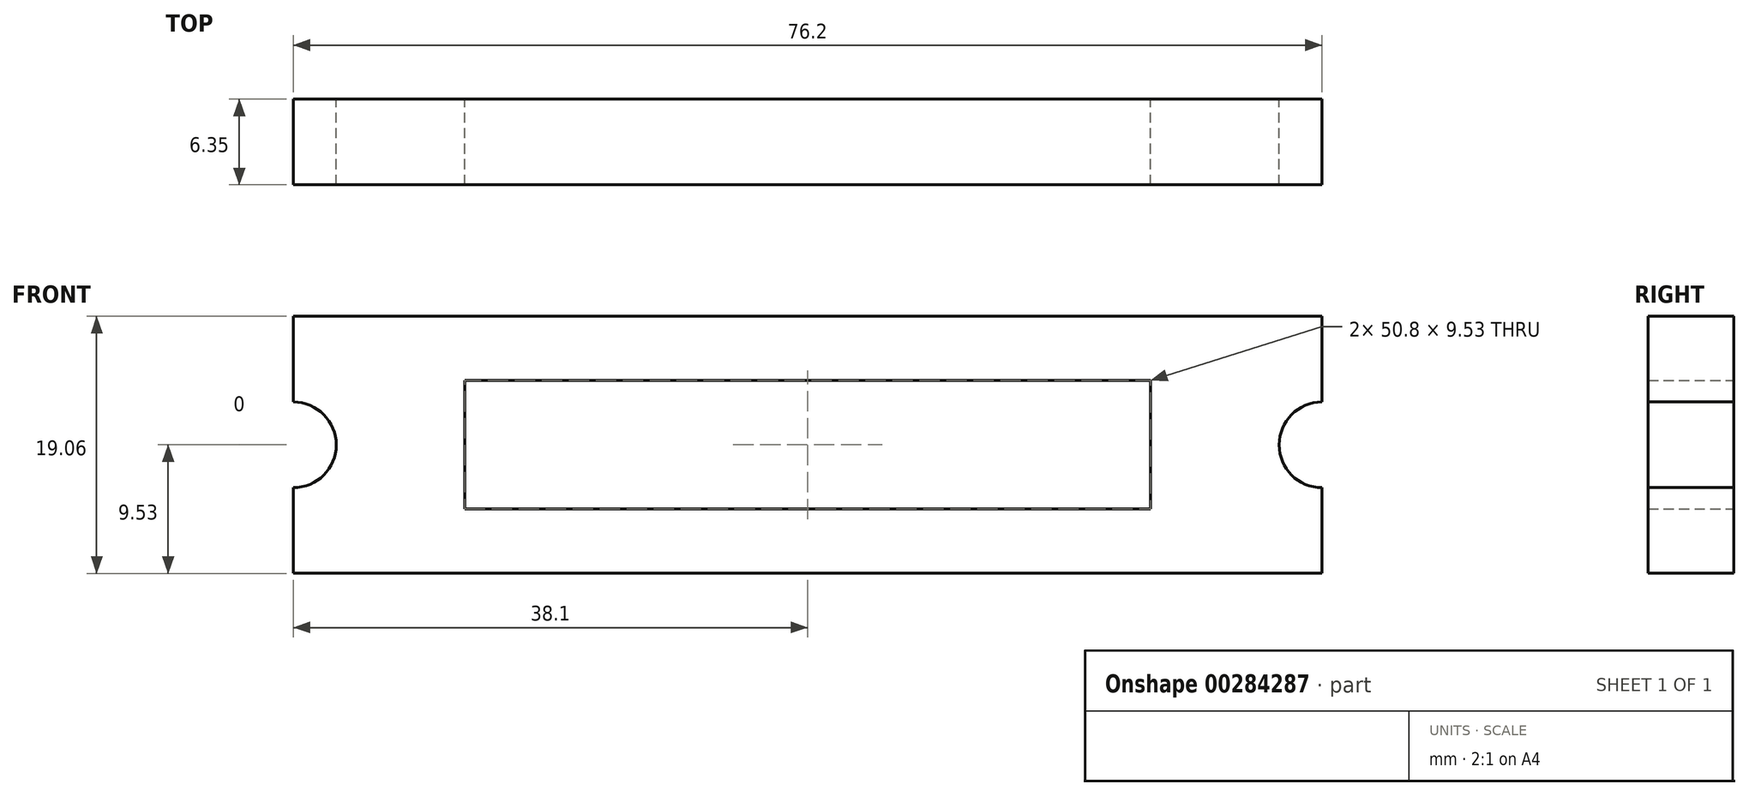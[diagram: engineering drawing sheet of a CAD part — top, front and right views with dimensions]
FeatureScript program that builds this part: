
annotation { "Feature Type Name" : "Feature", "Feature Type Description" : "" }
export const myFeature = defineFeature(function(context is Context, id is Id, definition is map)
    precondition{}
    {
        {
            var Q0;
            Q0=qCreatedBy(makeId("Front.planeOp"),FACE);
            var sketch = newSketch(context, id + "F0", { "sketchPlane" : qUnion([Q0])});
            skLineSegment(sketch, "E0.bottom", {"start": v(38.1, 9.53) * mm, "end": v(-38.1, 9.53) * mm});
            skLineSegment(sketch, "E0.top", {"start": v(38.1, -9.53) * mm, "end": v(-38.1, -9.53) * mm});
            skLineSegment(sketch, "E0.left", {"start": v(38.1, 9.53) * mm, "end": v(38.1, -9.53) * mm});
            skLineSegment(sketch, "E0.right", {"start": v(-38.1, 9.53) * mm, "end": v(-38.1, -9.53) * mm});
            skPoint(sketch, "E0.middle", {"position": v(0, 0) * mm});
            skArc(sketch, "E1", {"start": v(38.1, 9.53) * mm, "mid": v(47.62, 0) * mm, "end": v(38.1, -9.53) * mm});
            skArc(sketch, "E2", {"start": v(-38.1, -9.53) * mm, "mid": v(-47.62, 0) * mm, "end": v(-38.1, 9.53) * mm});
            skCircle(sketch, "E3", {"center": v(-38.1, 0) * mm, "radius": 3.18 * mm});
            skCircle(sketch, "E4", {"center": v(38.1, 0) * mm, "radius": 3.18 * mm});
            skLineSegment(sketch, "E5.bottom", {"start": v(25.4, 4.76) * mm, "end": v(-25.4, 4.76) * mm});
            skLineSegment(sketch, "E5.top", {"start": v(25.4, -4.76) * mm, "end": v(-25.4, -4.76) * mm});
            skLineSegment(sketch, "E5.left", {"start": v(25.4, 4.76) * mm, "end": v(25.4, -4.76) * mm});
            skLineSegment(sketch, "E5.right", {"start": v(-25.4, 4.76) * mm, "end": v(-25.4, -4.76) * mm});
            skSolve(sketch);
        }
        {
            var Q0;
            {var subQ0=sQuery(id+"F0.wireOp",EDGE,"E2");Q0=makeQuery(id+"F0.imprint","IMPRINT",FACE,{"disambiguationData":[TD([[makeQuery(id+"F0.imprint","IMPRINT",EDGE,{"derivedFrom":subQ0}),-1.0]])]});}
            var Q1;
            {var subQ5=sQuery(id+"F0.wireOp",EDGE,"E0.bottom");Q1=makeQuery(id+"F0.imprint","IMPRINT",FACE,{"disambiguationData":[TD([[makeQuery(id+"F0.imprint","IMPRINT",EDGE,{"derivedFrom":subQ5}),1.0]])]});}
            var Q2;
            {var subQ0=sQuery(id+"F0.wireOp",EDGE,"E1");Q2=makeQuery(id+"F0.imprint","IMPRINT",FACE,{"disambiguationData":[TD([[makeQuery(id+"F0.imprint","IMPRINT",EDGE,{"derivedFrom":subQ0}),-1.0]])]});}
            extrude(context, id + "F1", {"entities" : qUnion([Q0, Q1, Q2]), "depth" : 6.35 * mm});
        }
    });
